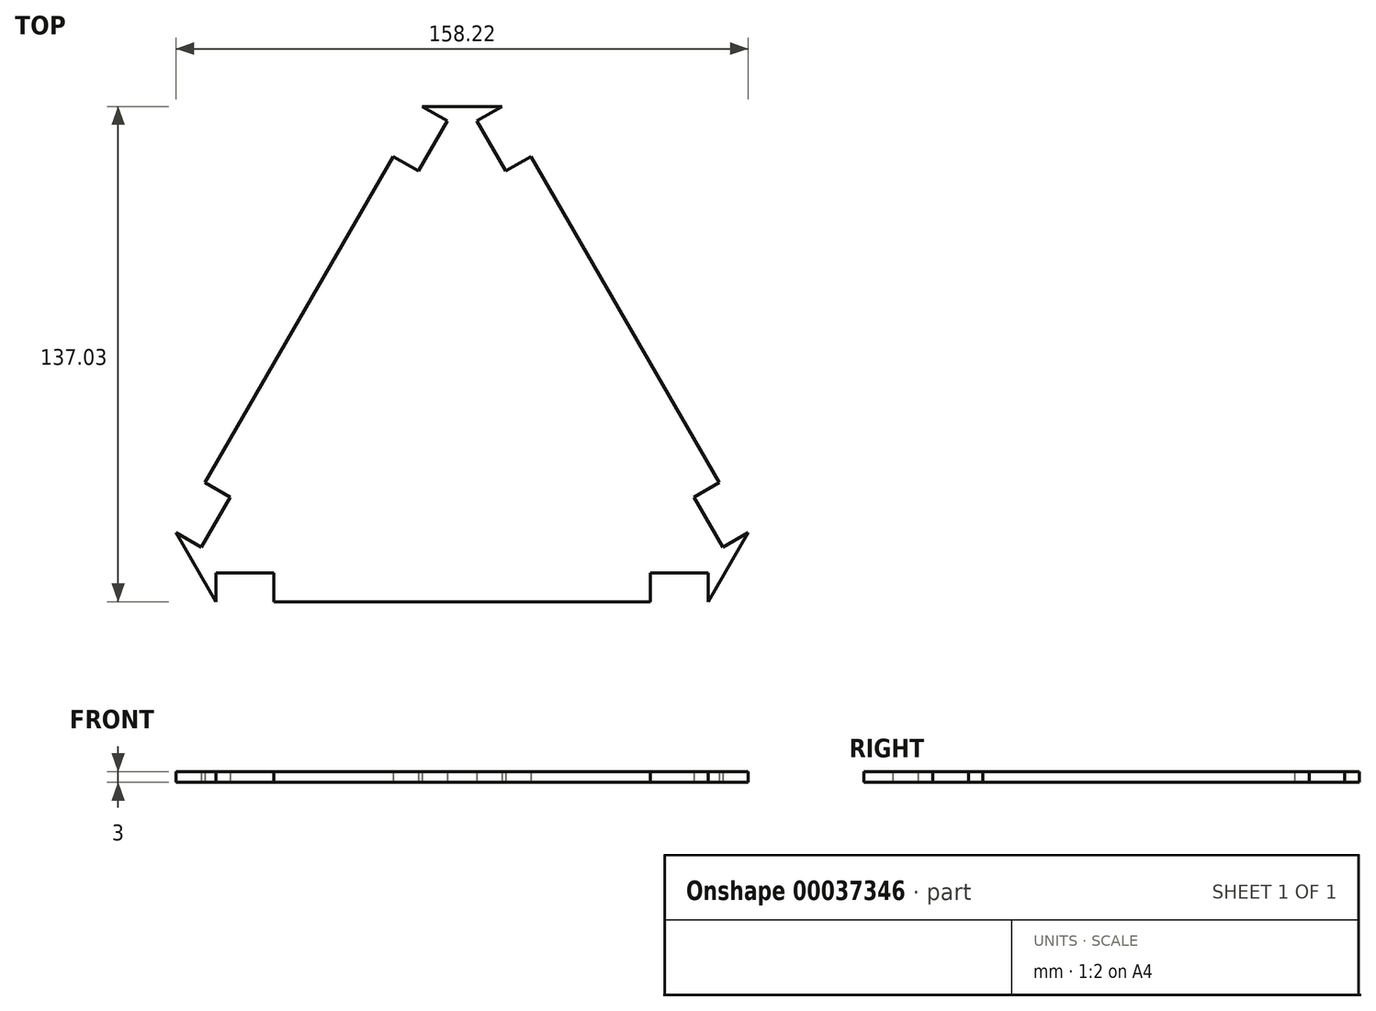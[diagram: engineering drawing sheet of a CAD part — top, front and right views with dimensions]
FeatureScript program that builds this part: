
annotation { "Feature Type Name" : "Feature", "Feature Type Description" : "" }
export const myFeature = defineFeature(function(context is Context, id is Id, definition is map)
    precondition{}
    {
        {
            var Q0;
            Q0=qCreatedBy(makeId("Top.planeOp"),FACE);
            var sketch = newSketch(context, id + "F0", { "sketchPlane" : qUnion([Q0])});
            skPoint(sketch, "E0.0.midPoint", {"position": v(0, 85) * mm});
            skLineSegment(sketch, "E1.0", {"start": v(0, 85) * mm, "end": v(73.61, -42.5) * mm});
            skLineSegment(sketch, "E1.1", {"start": v(73.61, -42.5) * mm, "end": v(-73.61, -42.5) * mm});
            skLineSegment(sketch, "E1.2", {"start": v(-73.61, -42.5) * mm, "end": v(0, 85) * mm});
            skCircle(sketch, "E2.cCircle", {"center": v(0, 0) * mm, "radius": 85 * mm, "construction": true});
            skLineSegment(sketch, "E2.0", {"start": v(-11, 85) * mm, "end": v(11, 85) * mm});
            skLineSegment(sketch, "E2.2", {"start": v(79.11, -32.97) * mm, "end": v(68.11, -52.03) * mm});
            skLineSegment(sketch, "E2.4", {"start": v(-68.11, -52.03) * mm, "end": v(-79.11, -32.97) * mm});
            skLineSegment(sketch, "E3", {"start": v(-11, 85) * mm, "end": v(-79.11, -32.97) * mm});
            skPoint(sketch, "E4.orphan", {"position": v(-87.92, -17.72) * mm});
            skLineSegment(sketch, "E5", {"start": v(0, 85) * mm, "end": v(0, 0) * mm});
            skLineSegment(sketch, "E6.0.MirrorCS", {"start": v(11, 85) * mm, "end": v(79.11, -32.97) * mm});
            skLineSegment(sketch, "E7", {"start": v(-68.11, -52.03) * mm, "end": v(68.11, -52.03) * mm});
            skLineSegment(sketch, "E8", {"start": v(-73.61, -42.5) * mm, "end": v(-68.11, -52.03) * mm});
            skLineSegment(sketch, "E9", {"start": v(-11, 85) * mm, "end": v(-19, 71.14) * mm});
            skLineSegment(sketch, "E10", {"start": v(-19, 71.14) * mm, "end": v(-12.07, 67.14) * mm});
            skLineSegment(sketch, "E11", {"start": v(-12.07, 67.14) * mm, "end": v(-4.07, 81) * mm});
            skLineSegment(sketch, "E12", {"start": v(-4.07, 81) * mm, "end": v(-11, 85) * mm});
            skLineSegment(sketch, "E13.0.MirrorCS", {"start": v(4.07, 81) * mm, "end": v(11, 85) * mm});
            skLineSegment(sketch, "E13.1.MirrorCS", {"start": v(19, 71.14) * mm, "end": v(12.07, 67.14) * mm});
            skLineSegment(sketch, "E13.2.MirrorCS", {"start": v(11, 85) * mm, "end": v(19, 71.14) * mm});
            skLineSegment(sketch, "E13.3.MirrorCS", {"start": v(12.07, 67.14) * mm, "end": v(4.07, 81) * mm});
            skLineSegment(sketch, "E14", {"start": v(45.06, 26.01) * mm, "end": v(-73.61, -42.5) * mm});
            skLineSegment(sketch, "E15", {"start": v(73.61, -42.5) * mm, "end": v(-45.06, 26.01) * mm});
            skLineSegment(sketch, "E16.0.MirrorCS", {"start": v(79.11, -32.97) * mm, "end": v(71.11, -19.12) * mm});
            skLineSegment(sketch, "E16.1.MirrorCS", {"start": v(72.18, -36.97) * mm, "end": v(79.11, -32.97) * mm});
            skLineSegment(sketch, "E16.2.MirrorCS", {"start": v(71.11, -19.12) * mm, "end": v(64.18, -23.12) * mm});
            skLineSegment(sketch, "E16.3.MirrorCS", {"start": v(64.18, -23.12) * mm, "end": v(72.18, -36.97) * mm});
            skLineSegment(sketch, "E17.0.MirrorCS", {"start": v(52.11, -44.03) * mm, "end": v(68.11, -44.03) * mm});
            skLineSegment(sketch, "E17.1.MirrorCS", {"start": v(68.11, -52.03) * mm, "end": v(52.11, -52.03) * mm});
            skLineSegment(sketch, "E17.2.MirrorCS", {"start": v(52.11, -52.03) * mm, "end": v(52.11, -44.03) * mm});
            skLineSegment(sketch, "E17.3.MirrorCS", {"start": v(68.11, -44.03) * mm, "end": v(68.11, -52.03) * mm});
            skLineSegment(sketch, "E18.0.MirrorCS", {"start": v(-72.18, -36.97) * mm, "end": v(-79.11, -32.97) * mm});
            skLineSegment(sketch, "E18.2.MirrorCS", {"start": v(-71.11, -19.12) * mm, "end": v(-64.18, -23.12) * mm});
            skLineSegment(sketch, "E18.3.MirrorCS", {"start": v(-64.18, -23.12) * mm, "end": v(-72.18, -36.97) * mm});
            skLineSegment(sketch, "E18.4.MirrorCS", {"start": v(0, 85) * mm, "end": v(-73.61, -42.5) * mm});
            skLineSegment(sketch, "E18.5.MirrorCS", {"start": v(-79.11, -32.97) * mm, "end": v(-71.11, -19.12) * mm});
            skLineSegment(sketch, "E18.7.MirrorCS", {"start": v(-79.11, -32.97) * mm, "end": v(-68.11, -52.03) * mm});
            skLineSegment(sketch, "E19.0.MirrorCS", {"start": v(-52.11, -52.03) * mm, "end": v(-52.11, -44.03) * mm});
            skLineSegment(sketch, "E19.1.MirrorCS", {"start": v(-52.11, -44.03) * mm, "end": v(-68.11, -44.03) * mm});
            skLineSegment(sketch, "E19.2.MirrorCS", {"start": v(-68.11, -44.03) * mm, "end": v(-68.11, -52.03) * mm});
            skLineSegment(sketch, "E19.3.MirrorCS", {"start": v(-68.11, -52.03) * mm, "end": v(-52.11, -52.03) * mm});
            skSolve(sketch);
        }
        {
            var Q0;
            {var subQ8=sQuery(id+"F0.wireOp",EDGE,"E10");Q0=makeQuery(id+"F0.imprint","IMPRINT",FACE,{"disambiguationData":[TD([[makeQuery(id+"F0.imprint","IMPRINT",EDGE,{"derivedFrom":subQ8}),-1.0]])]});}
            var Q1;
            {var subQ3=sQuery(id+"F0.wireOp",EDGE,"E5");Q1=makeQuery(id+"F0.imprint","IMPRINT",FACE,{"disambiguationData":[TD([[makeQuery(id+"F0.imprint","IMPRINT",EDGE,{"derivedFrom":subQ3}),-1.0]])]});}
            var Q2;
            {var subQ3=sQuery(id+"F0.wireOp",EDGE,"E5");Q2=makeQuery(id+"F0.imprint","IMPRINT",FACE,{"disambiguationData":[TD([[makeQuery(id+"F0.imprint","IMPRINT",EDGE,{"derivedFrom":subQ3}),1.0]])]});}
            var Q3;
            {var subQ5=sQuery(id+"F0.wireOp",EDGE,"E13.0.MirrorCS");Q3=makeQuery(id+"F0.imprint","IMPRINT",FACE,{"disambiguationData":[TD([[makeQuery(id+"F0.imprint","IMPRINT",EDGE,{"derivedFrom":subQ5}),1.0]])]});}
            var Q4;
            {var subQ1=sQuery(id+"F0.wireOp",EDGE,"E16.1.MirrorCS");Q4=makeQuery(id+"F0.imprint","IMPRINT",FACE,{"disambiguationData":[TD([[makeQuery(id+"F0.imprint","IMPRINT",EDGE,{"derivedFrom":subQ1}),-1.0]])]});}
            var Q5;
            {var subQ1=sQuery(id+"F0.wireOp",EDGE,"E14");var subQ3=sQuery(id+"F0.wireOp",EDGE,"E1.0");var subQ5=makeQuery(id+"F0.imprint","INTERSECT",VERTEX,{"derivedFrom":[subQ3,subQ1]});Q5=makeQuery(id+"F0.imprint","IMPRINT",FACE,{"disambiguationData":[TD([[makeQuery(id+"F0.imprint","IMPRINT",EDGE,{"disambiguationData":[TD([[subQ5,-1.0]])],"derivedFrom":subQ1}),1.0]])]});}
            var Q6;
            {var subQ3=sQuery(id+"F0.wireOp",EDGE,"E1.1");Q6=makeQuery(id+"F0.imprint","IMPRINT",FACE,{"disambiguationData":[TD([[makeQuery(id+"F0.imprint","IMPRINT",EDGE,{"derivedFrom":subQ3}),-1.0]])]});}
            var Q7;
            {var subQ0=sQuery(id+"F0.wireOp",EDGE,"E18.4.MirrorCS");var subQ1=sQuery(id+"F0.wireOp",EDGE,"E15");var subQ2=makeQuery(id+"F0.imprint","INTERSECT",VERTEX,{"derivedFrom":[subQ1,subQ0]});Q7=makeQuery(id+"F0.imprint","IMPRINT",FACE,{"disambiguationData":[TD([[makeQuery(id+"F0.imprint","IMPRINT",EDGE,{"disambiguationData":[TD([[subQ2,1.0]])],"derivedFrom":subQ1}),1.0]])]});}
            var Q8;
            {var subQ1=sQuery(id+"F0.wireOp",EDGE,"E18.0.MirrorCS");Q8=makeQuery(id+"F0.imprint","IMPRINT",FACE,{"disambiguationData":[TD([[makeQuery(id+"F0.imprint","IMPRINT",EDGE,{"derivedFrom":subQ1}),1.0]])]});}
            var Q9;
            {var subQ2=sQuery(id+"F0.wireOp",EDGE,"E1.1");Q9=makeQuery(id+"F0.imprint","IMPRINT",FACE,{"disambiguationData":[TD([[makeQuery(id+"F0.imprint","IMPRINT",EDGE,{"derivedFrom":subQ2}),1.0]])]});}
            extrude(context, id + "F1", {"entities" : qUnion([Q0, Q1, Q2, Q3, Q4, Q5, Q6, Q7, Q8, Q9]), "depth" : 3 * mm});
        }
    });
